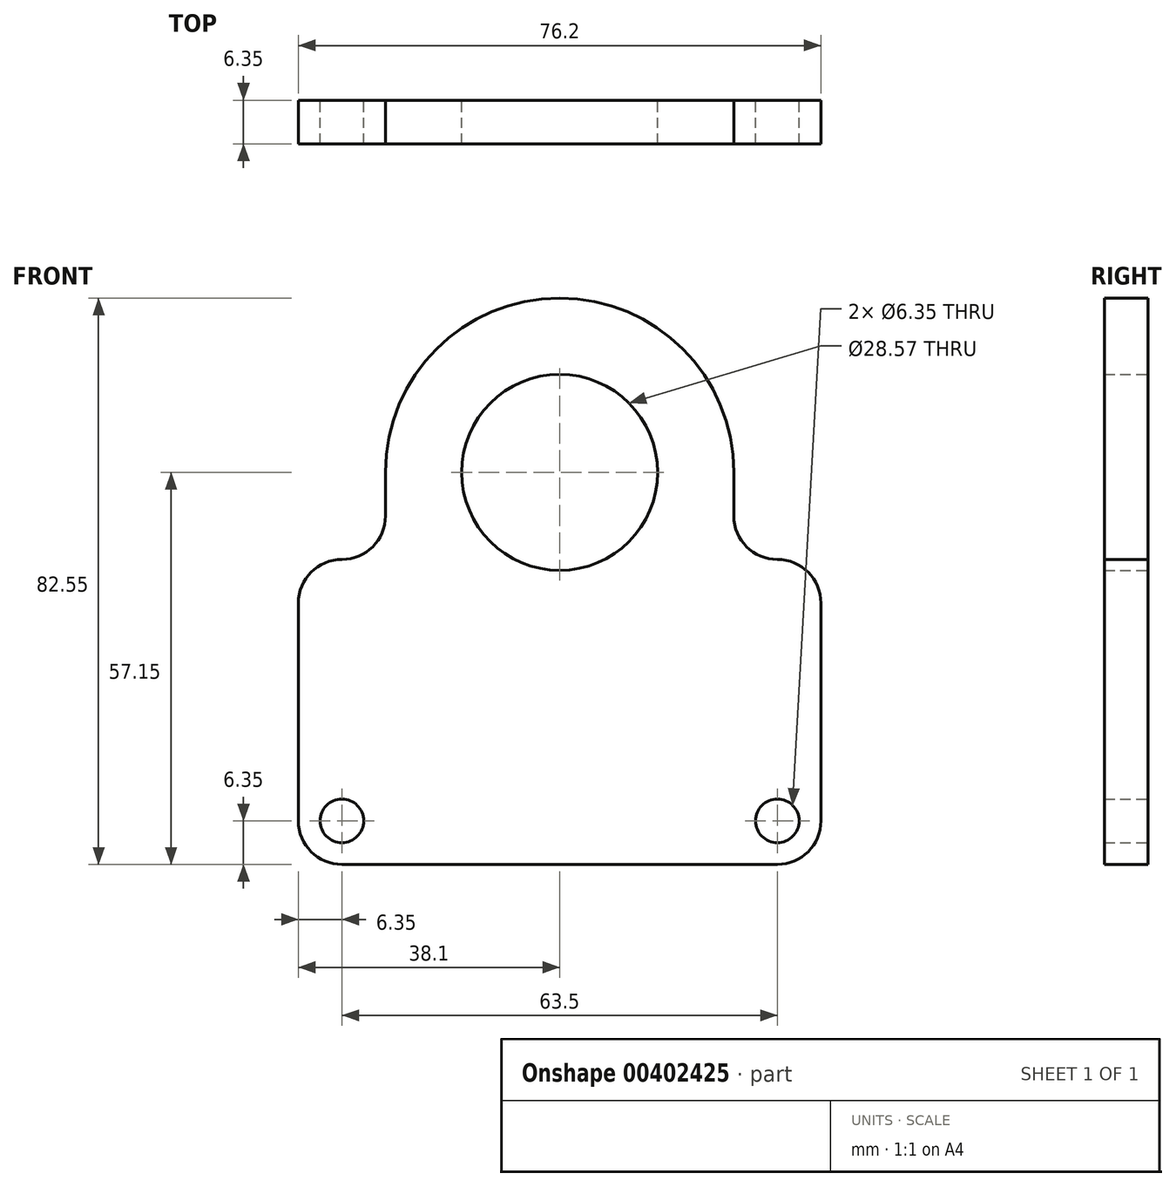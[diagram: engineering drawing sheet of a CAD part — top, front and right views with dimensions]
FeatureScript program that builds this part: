
annotation { "Feature Type Name" : "Feature", "Feature Type Description" : "" }
export const myFeature = defineFeature(function(context is Context, id is Id, definition is map)
    precondition{}
    {
        {
            var Q0;
            Q0=qCreatedBy(makeId("Front.planeOp"),FACE);
            var sketch = newSketch(context, id + "F0", { "sketchPlane" : qUnion([Q0])});
            skLineSegment(sketch, "E0.bottom", {"start": v(25.4, 0) * mm, "end": v(25.4, 0) * mm});
            skLineSegment(sketch, "E0.top", {"start": v(0, -63.5) * mm, "end": v(50.8, -63.5) * mm});
            skLineSegment(sketch, "E0.left", {"start": v(0, -25.4) * mm, "end": v(0, -31.75) * mm});
            skLineSegment(sketch, "E0.right", {"start": v(50.8, -25.4) * mm, "end": v(50.8, -31.75) * mm});
            skCircle(sketch, "E1", {"center": v(25.4, -25.4) * mm, "radius": 14.29 * mm});
            skCircle(sketch, "E2", {"center": v(-6.35, -76.2) * mm, "radius": 3.18 * mm});
            skCircle(sketch, "E3", {"center": v(57.15, -76.2) * mm, "radius": 3.18 * mm});
            skPoint(sketch, "E4.visualSharp", {"position": v(0, 0) * mm});
            skArc(sketch, "E4.filletArc", {"start": v(25.4, 0) * mm, "mid": v(7.44, -7.44) * mm, "end": v(0, -25.4) * mm});
            skPoint(sketch, "E5.visualSharp", {"position": v(50.8, 0) * mm});
            skArc(sketch, "E5.filletArc", {"start": v(50.8, -25.4) * mm, "mid": v(43.36, -7.44) * mm, "end": v(25.4, 0) * mm});
            skLineSegment(sketch, "E6.bottom", {"start": v(0, -63.5) * mm, "end": v(-6.35, -63.5) * mm});
            skLineSegment(sketch, "E6.top", {"start": v(-6.35, -38.1) * mm, "end": v(-6.35, -38.1) * mm});
            skLineSegment(sketch, "E6.left", {"start": v(0, -63.5) * mm, "end": v(0, -38.1) * mm});
            skLineSegment(sketch, "E6.right", {"start": v(-12.7, -57.15) * mm, "end": v(-12.7, -44.45) * mm});
            skLineSegment(sketch, "E7.bottom", {"start": v(50.8, -63.5) * mm, "end": v(57.15, -63.5) * mm});
            skLineSegment(sketch, "E7.top", {"start": v(57.15, -38.1) * mm, "end": v(57.15, -38.1) * mm});
            skLineSegment(sketch, "E7.left", {"start": v(50.8, -63.5) * mm, "end": v(50.8, -38.1) * mm});
            skLineSegment(sketch, "E7.right", {"start": v(63.5, -57.15) * mm, "end": v(63.5, -44.45) * mm});
            skPoint(sketch, "E8.visualSharp", {"position": v(-12.7, -38.1) * mm});
            skArc(sketch, "E8.filletArc", {"start": v(-6.35, -38.1) * mm, "mid": v(-10.84, -39.96) * mm, "end": v(-12.7, -44.45) * mm});
            skPoint(sketch, "E9.visualSharp", {"position": v(-12.7, -63.5) * mm});
            skArc(sketch, "E9.filletArc", {"start": v(-12.7, -57.15) * mm, "mid": v(-10.84, -61.64) * mm, "end": v(-6.35, -63.5) * mm});
            skPoint(sketch, "E10.visualSharp", {"position": v(63.5, -63.5) * mm});
            skArc(sketch, "E10.filletArc", {"start": v(57.15, -63.5) * mm, "mid": v(61.64, -61.64) * mm, "end": v(63.5, -57.15) * mm});
            skPoint(sketch, "E11.visualSharp", {"position": v(63.5, -38.1) * mm});
            skArc(sketch, "E11.filletArc", {"start": v(63.5, -44.45) * mm, "mid": v(61.64, -39.96) * mm, "end": v(57.15, -38.1) * mm});
            skArc(sketch, "E12.filletArc", {"start": v(-6.35, -38.1) * mm, "mid": v(-1.86, -36.24) * mm, "end": v(0, -31.75) * mm});
            skPoint(sketch, "E13.newPointA", {"position": v(50.8, -63.5) * mm});
            skArc(sketch, "E13.filletArc", {"start": v(50.8, -31.75) * mm, "mid": v(52.66, -36.24) * mm, "end": v(57.15, -38.1) * mm});
            skLineSegment(sketch, "E14.top", {"start": v(-6.35, -82.55) * mm, "end": v(57.15, -82.55) * mm});
            skLineSegment(sketch, "E14.left", {"start": v(-12.7, -57.15) * mm, "end": v(-12.7, -76.2) * mm});
            skLineSegment(sketch, "E14.right", {"start": v(63.5, -57.15) * mm, "end": v(63.5, -76.2) * mm});
            skPoint(sketch, "E15.visualSharp", {"position": v(-12.7, -82.55) * mm});
            skArc(sketch, "E15.filletArc", {"start": v(-12.7, -76.2) * mm, "mid": v(-10.84, -80.7) * mm, "end": v(-6.35, -82.55) * mm});
            skPoint(sketch, "E16.visualSharp", {"position": v(63.5, -82.55) * mm});
            skArc(sketch, "E16.filletArc", {"start": v(57.15, -82.55) * mm, "mid": v(61.64, -80.7) * mm, "end": v(63.5, -76.2) * mm});
            skSolve(sketch);
        }
        {
            var Q0;
            Q0=qSketchRegion(id+"F0",true);
            extrude(context, id + "F1", {"entities" : qUnion([Q0]), "depth" : 6.35 * mm});
        }
    });
